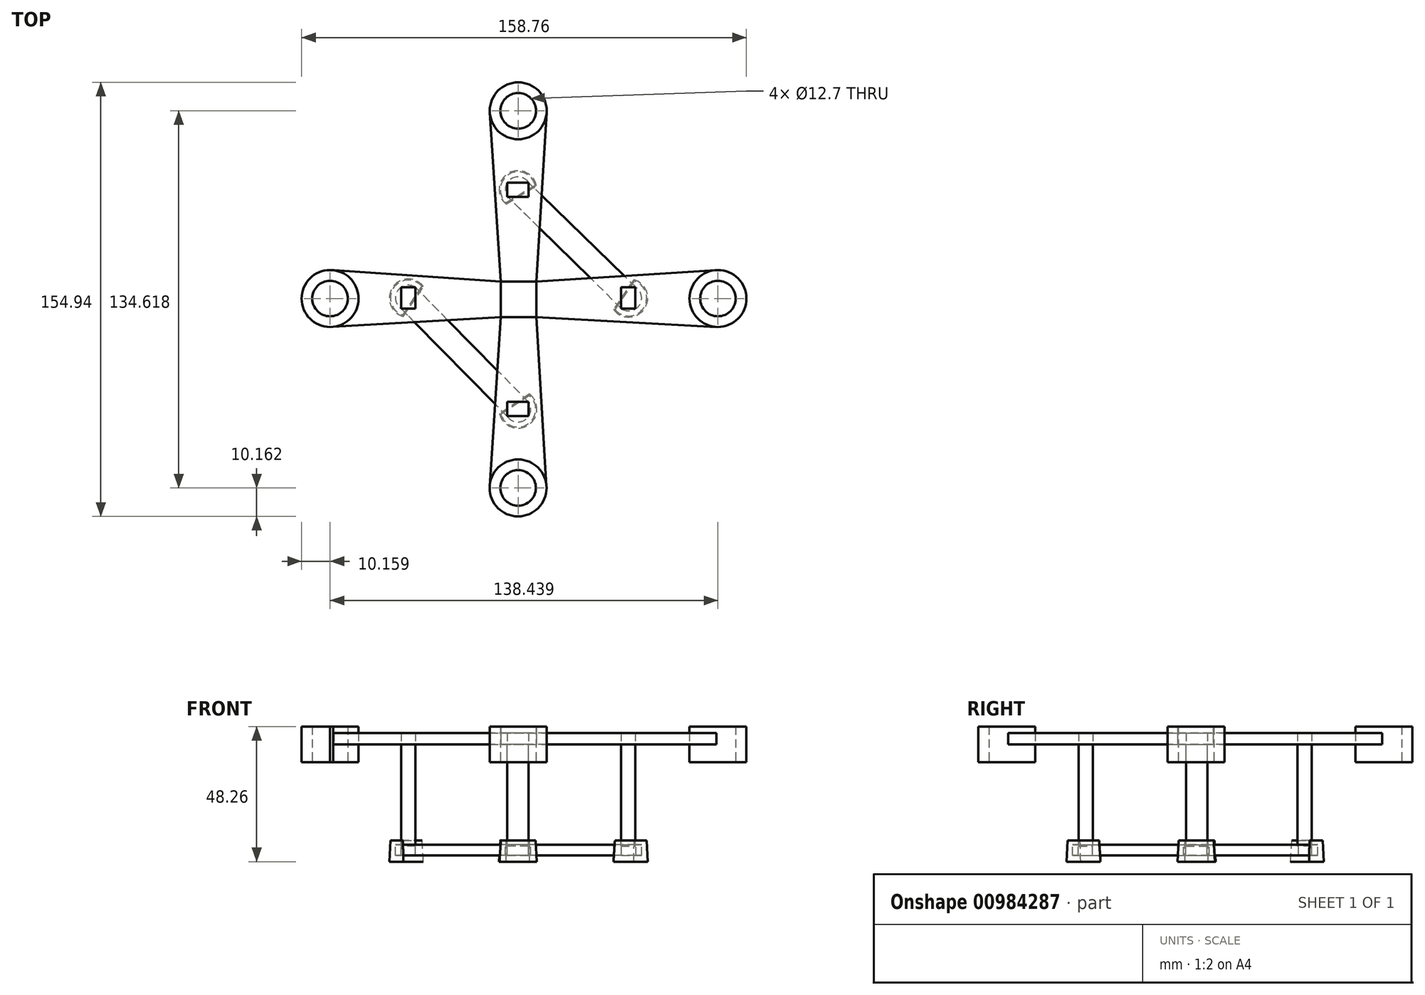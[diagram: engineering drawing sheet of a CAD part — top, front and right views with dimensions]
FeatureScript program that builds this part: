
annotation { "Feature Type Name" : "Feature", "Feature Type Description" : "" }
export const myFeature = defineFeature(function(context is Context, id is Id, definition is map)
    precondition{}
    {
        {
            var Q0;
            Q0=qCreatedBy(makeId("Top.planeOp"),FACE);
            var sketch = newSketch(context, id + "F0", { "sketchPlane" : qUnion([Q0])});
            skCircle(sketch, "E0", {"center": v(0, 67.31) * mm, "radius": 10.16 * mm});
            skCircle(sketch, "E1", {"center": v(0, 67.31) * mm, "radius": 6.35 * mm});
            skLineSegment(sketch, "E2.bottom", {"start": v(-6.21, -6.35) * mm, "end": v(6.49, -6.35) * mm});
            skLineSegment(sketch, "E2.top", {"start": v(-6.21, 6.35) * mm, "end": v(6.49, 6.35) * mm});
            skLineSegment(sketch, "E2.left", {"start": v(-6.21, -6.35) * mm, "end": v(-6.21, 6.35) * mm});
            skLineSegment(sketch, "E2.right", {"start": v(6.49, -6.35) * mm, "end": v(6.49, 6.35) * mm});
            skCircle(sketch, "E3", {"center": v(71.27, 0.3) * mm, "radius": 10.16 * mm});
            skCircle(sketch, "E4", {"center": v(71.27, 0.3) * mm, "radius": 6.35 * mm});
            skCircle(sketch, "E5", {"center": v(-0.06, -67.3) * mm, "radius": 10.16 * mm});
            skCircle(sketch, "E6", {"center": v(-0.06, -67.3) * mm, "radius": 6.35 * mm});
            skCircle(sketch, "E7", {"center": v(-67.17, 0.3) * mm, "radius": 10.16 * mm});
            skCircle(sketch, "E8", {"center": v(-67.17, 0.3) * mm, "radius": 6.35 * mm});
            skLineSegment(sketch, "E9", {"start": v(-67.17, -9.86) * mm, "end": v(-6.21, -6.35) * mm});
            skLineSegment(sketch, "E10", {"start": v(-67.17, 10.46) * mm, "end": v(-6.21, 6.35) * mm});
            skLineSegment(sketch, "E11", {"start": v(-10.14, 66.65) * mm, "end": v(-6.21, 6.35) * mm});
            skLineSegment(sketch, "E12", {"start": v(10.14, 66.7) * mm, "end": v(6.49, 6.35) * mm});
            skLineSegment(sketch, "E13", {"start": v(70.62, 10.44) * mm, "end": v(6.49, 6.35) * mm});
            skLineSegment(sketch, "E14", {"start": v(70.72, -9.84) * mm, "end": v(6.49, -6.35) * mm});
            skLineSegment(sketch, "E15", {"start": v(10.08, -66.7) * mm, "end": v(6.49, -6.35) * mm});
            skLineSegment(sketch, "E16", {"start": v(-10.2, -66.64) * mm, "end": v(-6.21, -6.35) * mm});
            skPoint(sketch, "E17.oppositeSnap0", {"position": v(8.29, -36.53) * mm});
            skLineSegment(sketch, "E17.bottom", {"start": v(3.64, -41.6) * mm, "end": v(-3.98, -41.6) * mm});
            skLineSegment(sketch, "E17.top", {"start": v(3.64, -36.53) * mm, "end": v(-3.98, -36.53) * mm});
            skLineSegment(sketch, "E17.left", {"start": v(3.64, -41.6) * mm, "end": v(3.64, -36.53) * mm});
            skLineSegment(sketch, "E17.right", {"start": v(-3.98, -41.6) * mm, "end": v(-3.98, -36.53) * mm});
            skLineSegment(sketch, "E18.MirrorCS", {"start": v(-3.98, 41.6) * mm, "end": v(-3.98, 36.53) * mm});
            skLineSegment(sketch, "E19.MirrorCS", {"start": v(3.64, 36.53) * mm, "end": v(-3.98, 36.53) * mm});
            skLineSegment(sketch, "E20.MirrorCS", {"start": v(3.64, 41.6) * mm, "end": v(-3.98, 41.6) * mm});
            skLineSegment(sketch, "E21.MirrorCS", {"start": v(3.64, 41.6) * mm, "end": v(3.64, 36.53) * mm});
            skLineSegment(sketch, "E22.bottom", {"start": v(36.66, -3.3) * mm, "end": v(36.66, 4.32) * mm});
            skLineSegment(sketch, "E22.top", {"start": v(41.74, -3.3) * mm, "end": v(41.74, 4.32) * mm});
            skLineSegment(sketch, "E22.left", {"start": v(36.66, -3.3) * mm, "end": v(41.74, -3.3) * mm});
            skLineSegment(sketch, "E22.right", {"start": v(36.66, 4.32) * mm, "end": v(41.74, 4.32) * mm});
            skLineSegment(sketch, "E23.MirrorCS", {"start": v(-41.74, -3.3) * mm, "end": v(-41.74, 4.32) * mm});
            skLineSegment(sketch, "E24.MirrorCS", {"start": v(-36.66, -3.3) * mm, "end": v(-41.74, -3.3) * mm});
            skLineSegment(sketch, "E25.MirrorCS", {"start": v(-36.66, 4.32) * mm, "end": v(-41.74, 4.32) * mm});
            skLineSegment(sketch, "E26.MirrorCS", {"start": v(-36.66, -3.3) * mm, "end": v(-36.66, 4.32) * mm});
            skSolve(sketch);
        }
        {
            var Q0;
            Q0=makeQuery(id+"F0.imprint","IMPRINT",FACE,{"disambiguationData":[TD([[makeQuery(id+"F0.imprint","IMPRINT",EDGE,{"derivedFrom":sQuery(id+"F0.wireOp",EDGE,"E2.bottom")}),1.0]])]});
            extrude(context, id + "F1", {"entities" : qUnion([Q0]), "depth" : 6.35 * mm, "offsetDistance" : 25.4 * mm});
        }
        {
            var Q0;
            Q0=makeQuery(id+"F0.imprint","IMPRINT",FACE,{"disambiguationData":[TD([[makeQuery(id+"F0.imprint","IMPRINT",EDGE,{"derivedFrom":sQuery(id+"F0.wireOp",EDGE,"E4")}),-1.0]])]});
            var Q1;
            Q1=makeQuery(id+"F0.imprint","IMPRINT",FACE,{"disambiguationData":[TD([[makeQuery(id+"F0.imprint","IMPRINT",EDGE,{"derivedFrom":sQuery(id+"F0.wireOp",EDGE,"E1")}),-1.0]])]});
            var Q2;
            Q2=makeQuery(id+"F0.imprint","IMPRINT",FACE,{"disambiguationData":[TD([[makeQuery(id+"F0.imprint","IMPRINT",EDGE,{"derivedFrom":sQuery(id+"F0.wireOp",EDGE,"E8")}),-1.0]])]});
            var Q3;
            Q3=makeQuery(id+"F0.imprint","IMPRINT",FACE,{"disambiguationData":[TD([[makeQuery(id+"F0.imprint","IMPRINT",EDGE,{"derivedFrom":sQuery(id+"F0.wireOp",EDGE,"E6")}),-1.0]])]});
            extrude(context, id + "F2", {"entities" : qUnion([Q0, Q1, Q2, Q3]), "endBound" : BoundingType.SYMMETRIC, "depth" : 12.7 * mm, "offsetDistance" : 25.4 * mm});
        }
        {
            var Q0;
            Q0=makeQuery(id+"F0.imprint","IMPRINT",FACE,{"disambiguationData":[TD([[makeQuery(id+"F0.imprint","IMPRINT",EDGE,{"derivedFrom":sQuery(id+"F0.wireOp",EDGE,"E2.right")}),-1.0]])]});
            var Q1;
            Q1=makeQuery(id+"F0.imprint","IMPRINT",FACE,{"disambiguationData":[TD([[makeQuery(id+"F0.imprint","IMPRINT",EDGE,{"derivedFrom":sQuery(id+"F0.wireOp",EDGE,"E2.top")}),1.0]])]});
            var Q2;
            {var subQ0=sQuery(id+"F0.wireOp",EDGE,"E2.left");Q2=makeQuery(id+"F0.imprint","IMPRINT",FACE,{"disambiguationData":[TD([[makeQuery(id+"F0.imprint","IMPRINT",EDGE,{"derivedFrom":subQ0}),1.0]])]});}
            var Q3;
            Q3=makeQuery(id+"F0.imprint","IMPRINT",FACE,{"disambiguationData":[TD([[makeQuery(id+"F0.imprint","IMPRINT",EDGE,{"derivedFrom":sQuery(id+"F0.wireOp",EDGE,"E2.bottom")}),-1.0]])]});
            extrude(context, id + "F3", {"entities" : qUnion([Q0, Q1, Q2, Q3]), "depth" : 4.06 * mm, "offsetDistance" : 25.4 * mm});
        }
        {
            var Q0;
            Q0=makeQuery(id+"F0.imprint","IMPRINT",FACE,{"disambiguationData":[TD([[makeQuery(id+"F0.imprint","IMPRINT",EDGE,{"derivedFrom":sQuery(id+"F0.wireOp",EDGE,"E18.MirrorCS")}),1.0]])]});
            var Q1;
            Q1=makeQuery(id+"F0.imprint","IMPRINT",FACE,{"disambiguationData":[TD([[makeQuery(id+"F0.imprint","IMPRINT",EDGE,{"derivedFrom":sQuery(id+"F0.wireOp",EDGE,"E22.bottom")}),-1.0]])]});
            var Q2;
            Q2=makeQuery(id+"F0.imprint","IMPRINT",FACE,{"disambiguationData":[TD([[makeQuery(id+"F0.imprint","IMPRINT",EDGE,{"derivedFrom":sQuery(id+"F0.wireOp",EDGE,"E23.MirrorCS")}),-1.0]])]});
            var Q3;
            Q3=makeQuery(id+"F0.imprint","IMPRINT",FACE,{"disambiguationData":[TD([[makeQuery(id+"F0.imprint","IMPRINT",EDGE,{"derivedFrom":sQuery(id+"F0.wireOp",EDGE,"E17.bottom")}),-1.0]])]});
            extrude(context, id + "F4", {"entities" : qUnion([Q0, Q1, Q2, Q3]), "oppositeDirection" : true, "depth" : 36.32 * mm, "offsetDistance" : 25.4 * mm});
        }
        {
            var Q0;
            Q0=qCreatedBy(makeId("Top.planeOp"),FACE);
            var sketch = newSketch(context, id + "F5", { "sketchPlane" : qUnion([Q0])});
            skLineSegment(sketch, "E27", {"start": v(-41.8, -3.32) * mm, "end": v(-41.8, 4.29) * mm});
            skLineSegment(sketch, "E28", {"start": v(-41.8, 4.29) * mm, "end": v(-36.71, 4.29) * mm});
            skLineSegment(sketch, "E29", {"start": v(-36.71, 4.29) * mm, "end": v(-36.71, -3.32) * mm});
            skLineSegment(sketch, "E30", {"start": v(-36.71, -3.32) * mm, "end": v(-41.8, -3.32) * mm});
            skLineSegment(sketch, "E31", {"start": v(-3.94, -41.71) * mm, "end": v(3.7, -41.71) * mm});
            skLineSegment(sketch, "E32", {"start": v(3.7, -41.71) * mm, "end": v(3.7, -36.65) * mm});
            skLineSegment(sketch, "E33", {"start": v(3.7, -36.65) * mm, "end": v(-3.94, -36.65) * mm});
            skLineSegment(sketch, "E34", {"start": v(-3.94, -36.65) * mm, "end": v(-3.94, -41.71) * mm});
            skLineSegment(sketch, "E35", {"start": v(3.7, -36.65) * mm, "end": v(-36.71, 4.29) * mm});
            skLineSegment(sketch, "E36", {"start": v(-3.94, -41.71) * mm, "end": v(-41.8, -3.32) * mm});
            skLineSegment(sketch, "E37", {"start": v(42, 4.29) * mm, "end": v(42, -3.32) * mm});
            skLineSegment(sketch, "E38", {"start": v(42, -3.32) * mm, "end": v(36.84, -3.32) * mm});
            skLineSegment(sketch, "E39", {"start": v(36.84, -3.32) * mm, "end": v(36.84, 4.29) * mm});
            skLineSegment(sketch, "E40", {"start": v(36.84, 4.29) * mm, "end": v(42, 4.29) * mm});
            skLineSegment(sketch, "E41", {"start": v(3.78, 41.55) * mm, "end": v(3.78, 36.83) * mm});
            skLineSegment(sketch, "E42", {"start": v(3.78, 36.83) * mm, "end": v(-3.95, 36.83) * mm});
            skLineSegment(sketch, "E43", {"start": v(-3.95, 36.83) * mm, "end": v(-3.95, 41.55) * mm});
            skLineSegment(sketch, "E44", {"start": v(-3.95, 41.55) * mm, "end": v(3.78, 41.55) * mm});
            skLineSegment(sketch, "E45", {"start": v(42, 4.29) * mm, "end": v(3.78, 41.55) * mm});
            skLineSegment(sketch, "E46", {"start": v(36.84, -3.32) * mm, "end": v(-3.95, 36.83) * mm});
            skArc(sketch, "E47", {"start": v(-3.94, -41.71) * mm, "mid": v(2.4, -43) * mm, "end": v(3.7, -36.65) * mm});
            skArc(sketch, "E48", {"start": v(-36.71, 4.29) * mm, "mid": v(-43.06, 3.02) * mm, "end": v(-41.8, -3.32) * mm});
            skArc(sketch, "E49", {"start": v(36.84, -3.32) * mm, "mid": v(43.22, -2.1) * mm, "end": v(42, 4.29) * mm});
            skArc(sketch, "E50", {"start": v(3.78, 41.55) * mm, "mid": v(-2.45, 43.06) * mm, "end": v(-3.95, 36.83) * mm});
            skLineSegment(sketch, "E51", {"start": v(-3.94, -41.71) * mm, "end": v(3.7, -36.65) * mm});
            skLineSegment(sketch, "E52", {"start": v(36.84, -3.32) * mm, "end": v(42, 4.29) * mm});
            skLineSegment(sketch, "E53", {"start": v(3.78, 41.55) * mm, "end": v(-3.95, 36.83) * mm});
            skLineSegment(sketch, "E54", {"start": v(-41.8, -3.32) * mm, "end": v(-36.71, 4.29) * mm});
            skSolve(sketch);
        }
        {
            var Q0;
            Q0 = qSketchRegion(id + "F5", true);
            extrude(context, id + "F6", {"entities" : qUnion([Q0]), "oppositeDirection" : true, "depth" : 39.62 * mm, "offsetDistance" : 25.4 * mm, "hasSecondDirection" : true, "secondDirectionOppositeDirection" : true, "secondDirectionDepth" : 35.81 * mm});
        }
        {
            var Q0;
            {var subQ0=sQuery(id+"F5.wireOp",EDGE,"E37");Q0=makeQuery(id+"F5.imprint","IMPRINT",FACE,{"disambiguationData":[TD([[makeQuery(id+"F5.imprint","IMPRINT",EDGE,{"derivedFrom":subQ0}),1.0]])]});}
            var Q1;
            {var subQ0=sQuery(id+"F5.wireOp",EDGE,"E38");Q1=makeQuery(id+"F5.imprint","IMPRINT",FACE,{"disambiguationData":[TD([[makeQuery(id+"F5.imprint","IMPRINT",EDGE,{"derivedFrom":subQ0}),1.0]])]});}
            var Q2;
            Q2=makeQuery(id+"F5.imprint","IMPRINT",FACE,{"disambiguationData":[TD([[makeQuery(id+"F5.imprint","IMPRINT",EDGE,{"derivedFrom":sQuery(id+"F5.wireOp",EDGE,"E37")}),-1.0]])]});
            var Q3;
            Q3=makeQuery(id+"F5.imprint","IMPRINT",FACE,{"disambiguationData":[TD([[makeQuery(id+"F5.imprint","IMPRINT",EDGE,{"derivedFrom":sQuery(id+"F5.wireOp",EDGE,"E31")}),1.0]])]});
            var Q4;
            Q4=makeQuery(id+"F5.imprint","IMPRINT",FACE,{"disambiguationData":[TD([[makeQuery(id+"F5.imprint","IMPRINT",EDGE,{"derivedFrom":sQuery(id+"F5.wireOp",EDGE,"E27")}),-1.0]])]});
            var Q5;
            Q5=makeQuery(id+"F5.imprint","IMPRINT",FACE,{"disambiguationData":[TD([[makeQuery(id+"F5.imprint","IMPRINT",EDGE,{"derivedFrom":sQuery(id+"F5.wireOp",EDGE,"E43")}),-1.0]])]});
            var Q6;
            {var subQ0=sQuery(id+"F5.wireOp",EDGE,"E31");Q6=makeQuery(id+"F5.imprint","IMPRINT",FACE,{"disambiguationData":[TD([[makeQuery(id+"F5.imprint","IMPRINT",EDGE,{"derivedFrom":subQ0}),-1.0]])]});}
            var Q7;
            {var subQ0=sQuery(id+"F5.wireOp",EDGE,"E32");Q7=makeQuery(id+"F5.imprint","IMPRINT",FACE,{"disambiguationData":[TD([[makeQuery(id+"F5.imprint","IMPRINT",EDGE,{"derivedFrom":subQ0}),-1.0]])]});}
            var Q8;
            {var subQ0=sQuery(id+"F5.wireOp",EDGE,"E27");Q8=makeQuery(id+"F5.imprint","IMPRINT",FACE,{"disambiguationData":[TD([[makeQuery(id+"F5.imprint","IMPRINT",EDGE,{"derivedFrom":subQ0}),1.0]])]});}
            var Q9;
            {var subQ0=sQuery(id+"F5.wireOp",EDGE,"E28");Q9=makeQuery(id+"F5.imprint","IMPRINT",FACE,{"disambiguationData":[TD([[makeQuery(id+"F5.imprint","IMPRINT",EDGE,{"derivedFrom":subQ0}),1.0]])]});}
            var Q10;
            {var subQ0=sQuery(id+"F5.wireOp",EDGE,"E44");Q10=makeQuery(id+"F5.imprint","IMPRINT",FACE,{"disambiguationData":[TD([[makeQuery(id+"F5.imprint","IMPRINT",EDGE,{"derivedFrom":subQ0}),1.0]])]});}
            var Q11;
            {var subQ0=sQuery(id+"F5.wireOp",EDGE,"E43");Q11=makeQuery(id+"F5.imprint","IMPRINT",FACE,{"disambiguationData":[TD([[makeQuery(id+"F5.imprint","IMPRINT",EDGE,{"derivedFrom":subQ0}),1.0]])]});}
            extrude(context, id + "F7", {"entities" : qUnion([Q0, Q1, Q2, Q3, Q4, Q5, Q6, Q7, Q8, Q9, Q10, Q11]), "oppositeDirection" : true, "depth" : 41.9 * mm, "offsetDistance" : 25.4 * mm, "hasDraft" : true, "draftAngle" : 3 * degree, "hasSecondDirection" : true, "secondDirectionOppositeDirection" : true, "secondDirectionDepth" : 34.3 * mm});
        }
    });
